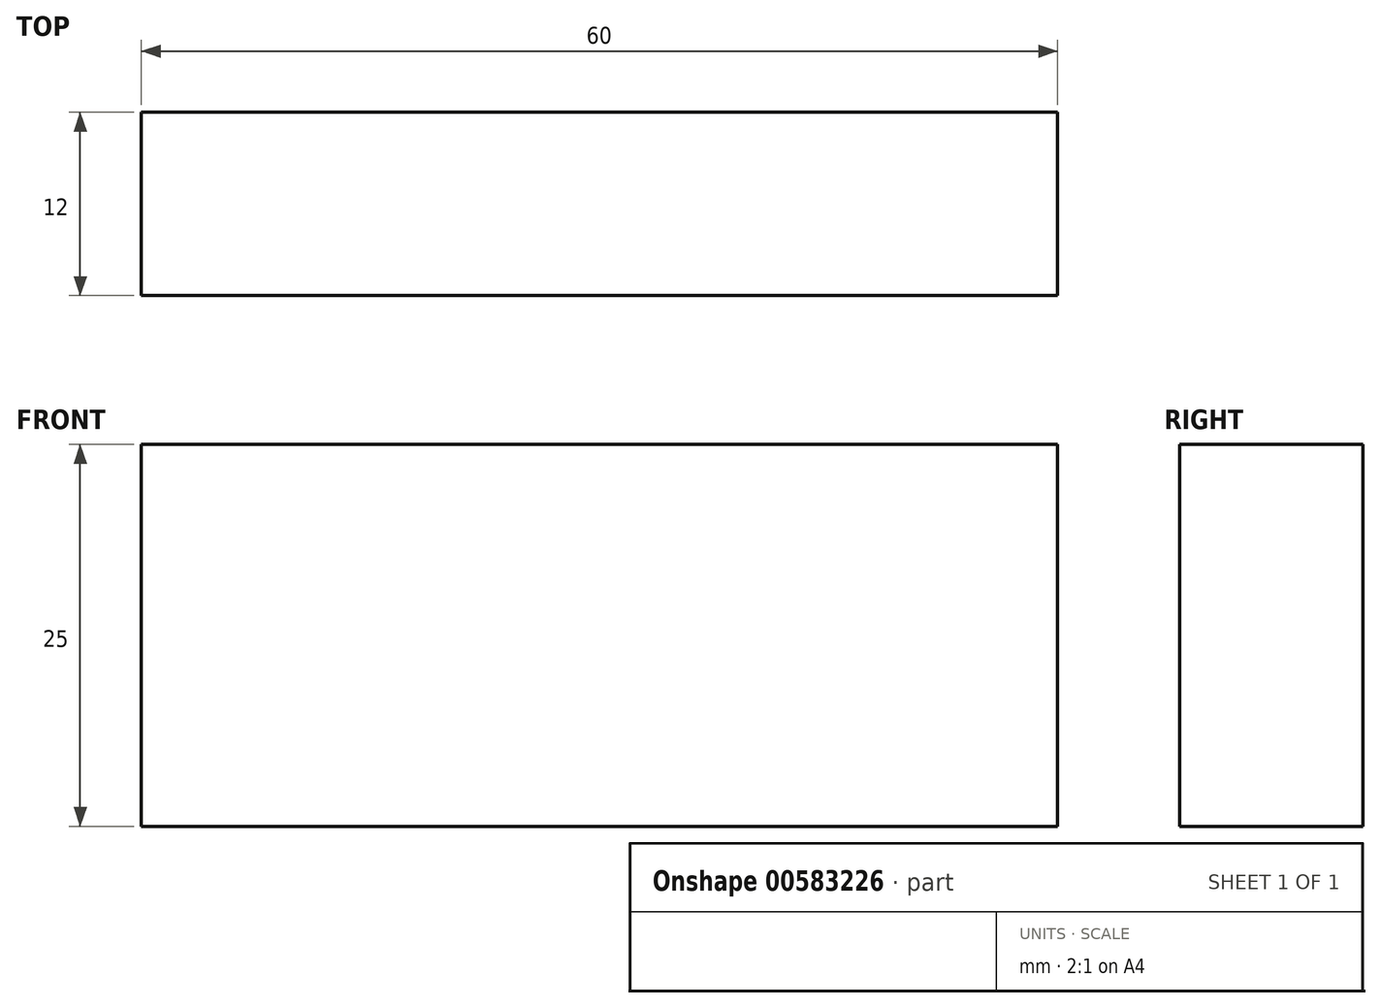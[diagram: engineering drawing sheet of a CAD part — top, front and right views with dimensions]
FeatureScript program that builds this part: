
annotation { "Feature Type Name" : "Feature", "Feature Type Description" : "" }
export const myFeature = defineFeature(function(context is Context, id is Id, definition is map)
    precondition{}
    {
        {
            var Q0;
            Q0=qCreatedBy(makeId("Front.planeOp"),FACE);
            var sketch = newSketch(context, id + "F0", { "sketchPlane" : qUnion([Q0])});
            skLineSegment(sketch, "E0.bottom", {"start": v(30, -12.5) * mm, "end": v(-30, -12.5) * mm});
            skLineSegment(sketch, "E0.top", {"start": v(30, 12.5) * mm, "end": v(-30, 12.5) * mm});
            skLineSegment(sketch, "E0.left", {"start": v(30, -12.5) * mm, "end": v(30, 12.5) * mm});
            skLineSegment(sketch, "E0.right", {"start": v(-30, -12.5) * mm, "end": v(-30, 12.5) * mm});
            skPoint(sketch, "E0.middle", {"position": v(0, 0) * mm});
            skSolve(sketch);
        }
        {
            var Q0;
            Q0=qSketchRegion(id+"F0",true);
            extrude(context, id + "F1", {"entities" : qUnion([Q0]), "endBound" : BoundingType.SYMMETRIC, "depth" : 12 * mm});
        }
    });
